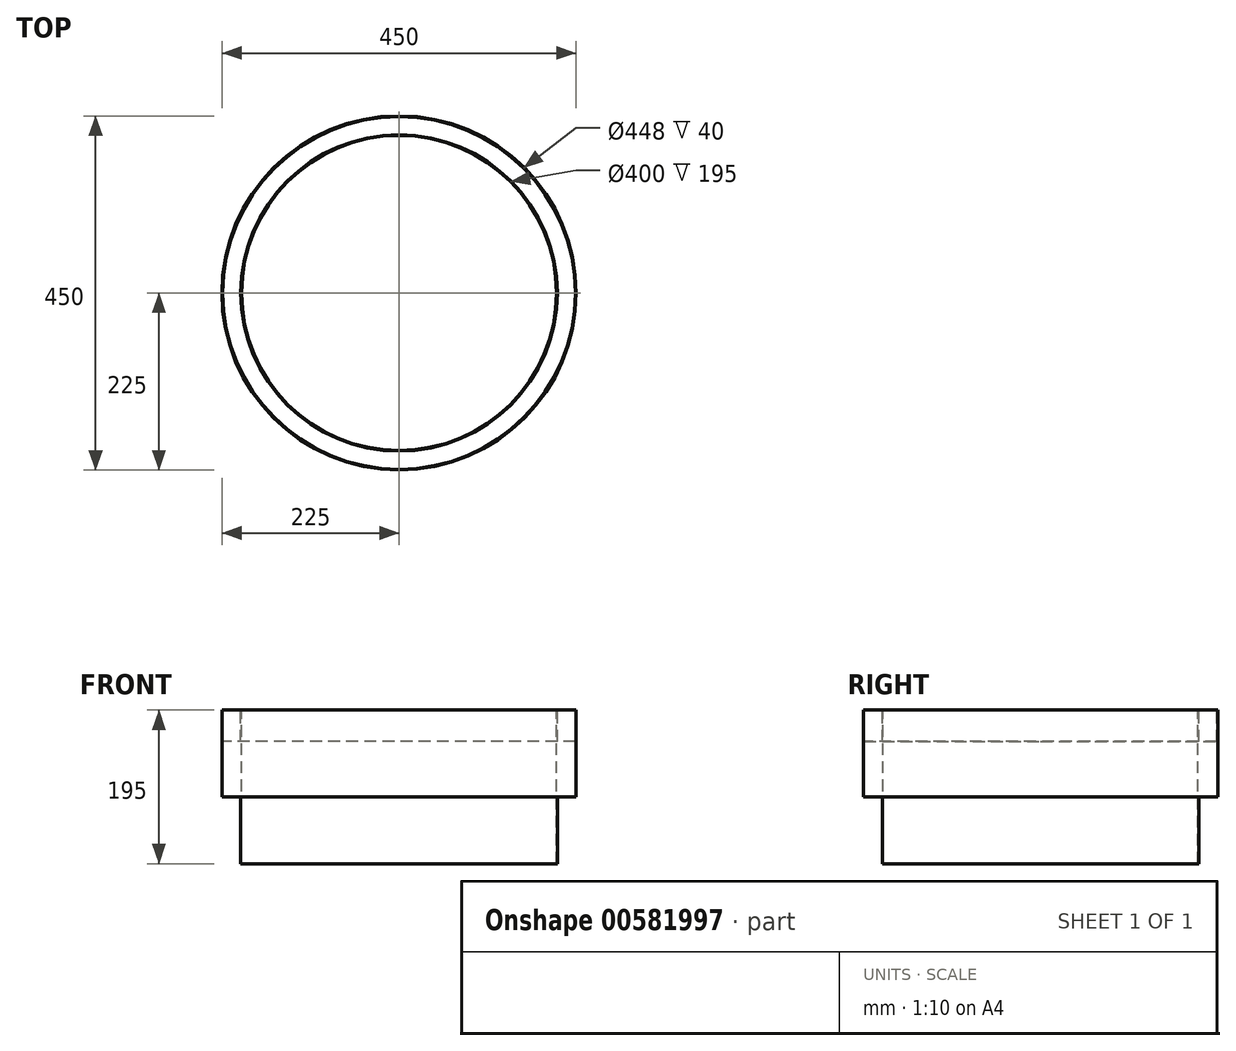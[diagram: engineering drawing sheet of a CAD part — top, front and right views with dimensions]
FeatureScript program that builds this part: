
annotation { "Feature Type Name" : "Feature", "Feature Type Description" : "" }
export const myFeature = defineFeature(function(context is Context, id is Id, definition is map)
    precondition{}
    {
        {
            var Q0;
            Q0=qCreatedBy(makeId("Front.planeOp"),FACE);
            var sketch = newSketch(context, id + "F0", { "sketchPlane" : qUnion([Q0])});
            skLineSegment(sketch, "E0", {"start": v(0, 710.75) * mm, "end": v(0, -704.58) * mm, "construction": true});
            skLineSegment(sketch, "E1", {"start": v(-200, 215.65) * mm, "end": v(-200, 410.65) * mm});
            skLineSegment(sketch, "E2", {"start": v(-200, 410.65) * mm, "end": v(-201, 410.65) * mm});
            skLineSegment(sketch, "E3", {"start": v(-224, 410.65) * mm, "end": v(-225, 410.65) * mm});
            skLineSegment(sketch, "E4", {"start": v(-225, 410.65) * mm, "end": v(-225, 300.65) * mm});
            skLineSegment(sketch, "E5", {"start": v(-225, 300.65) * mm, "end": v(-201, 300.65) * mm});
            skLineSegment(sketch, "E6", {"start": v(-201, 300.65) * mm, "end": v(-201, 215.65) * mm});
            skLineSegment(sketch, "E7", {"start": v(-224, 410.65) * mm, "end": v(-224, 370.65) * mm});
            skLineSegment(sketch, "E8", {"start": v(-224, 370.65) * mm, "end": v(-201, 370.65) * mm});
            skLineSegment(sketch, "E9", {"start": v(-201, 370.65) * mm, "end": v(-201, 410.65) * mm});
            skLineSegment(sketch, "E10", {"start": v(-201, 215.65) * mm, "end": v(-200, 215.65) * mm});
            skSolve(sketch);
        }
        {
            var Q0;
            Q0=qSketchRegion(id+"F0",true);
            var Q1;
            Q1=sQuery(id+"F0.wireOp",EDGE,"E0");
            revolve(context, id + "F1", {"entities" : qUnion([Q0]), "axis" : qUnion([Q1]), "revolveType" : RevolveType.FULL});
        }
    });
